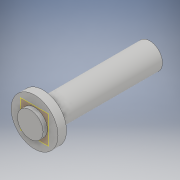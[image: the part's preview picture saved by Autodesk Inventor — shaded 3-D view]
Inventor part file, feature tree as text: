
AUTODESK INVENTOR PART (.ipt)
format: ipt  version: 2018 (Build 220112000, 112)  size: 105,984 bytes
history: native  units: in
note: dims shown in document units (in); Inventor stores cm internally (conversion verified against a paired STEP export)
features: extrude x2, sketch x2, plane x1
ambient origin geometry x8: Origin, YZ Plane, XZ Plane, XY Plane, X Axis, Y Axis, Z Axis, Center Point
bodies: Solid1 (feature_tree)
feature tree (5):
  extrude  "Extrusion1"  Depth=14.0in TaperAngle=0.0deg
  plane  "Work Plane1"
  extrude  "Extrusion2"  Depth=1.0in
  sketch  "Sketch1"  dims[d0=3.0in d1=14.0in d2=0.0in]
  sketch  "Sketch2"  dims[d3=-0.5in d4=5.5in d5=1.0in d6=0.0in]
